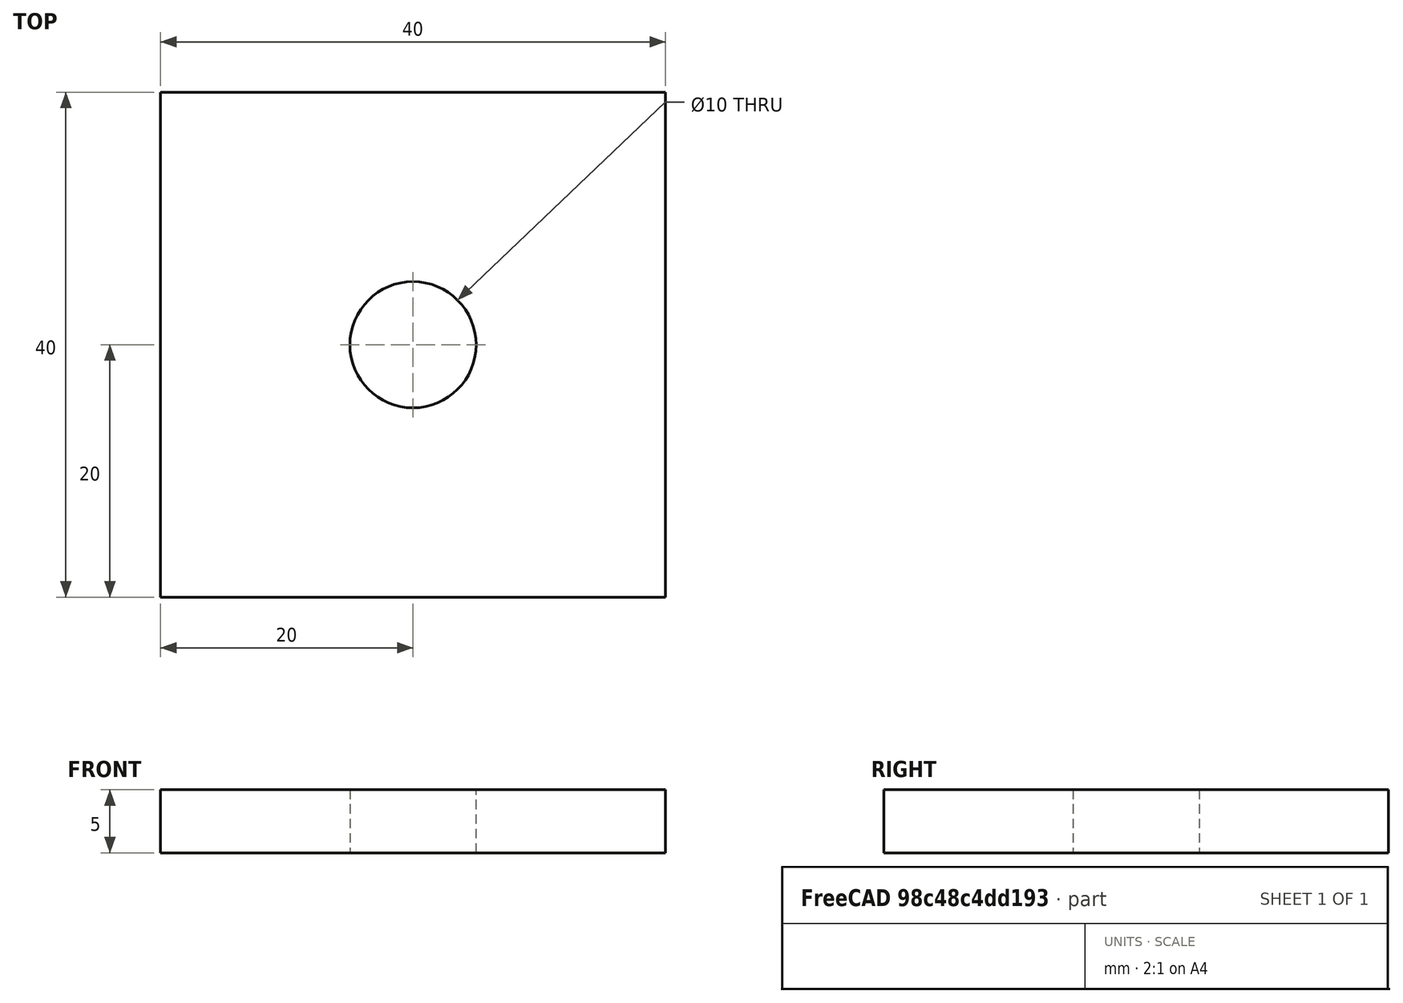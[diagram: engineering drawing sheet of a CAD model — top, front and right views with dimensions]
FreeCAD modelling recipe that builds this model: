
FCSTD DOCUMENT  (FreeCAD 0.20R29177 +233 (Git))
Label: L4-Ej3
License: Creative Commons Attribution-ShareAlike
LicenseURL: http://creativecommons.org/licenses/by-sa/4.0/
objects: Part::Extrusion×2, Sketcher::SketchObject×1
note: 3 computed .brp shape members not serialized (recipe doc carries the construction recipe); baked Part::Feature solids carry a one-line shape summary decoded from their .brp

FEATURE [Sketcher::SketchObject] Sketch
  FullyConstrained = true
  sketch-geometry (5):
    g0: LineSegment StartX=-20 StartY=20 StartZ=0 EndX=20 EndY=20 EndZ=0
    g1: LineSegment StartX=20 StartY=20 StartZ=0 EndX=20 EndY=-20 EndZ=0
    g2: LineSegment StartX=20 StartY=-20 StartZ=0 EndX=-20 EndY=-20 EndZ=0
    g3: LineSegment StartX=-20 StartY=-20 StartZ=0 EndX=-20 EndY=20 EndZ=0
    g4: Circle CenterX=0 CenterY=0 CenterZ=0 NormalX=0 NormalY=0 NormalZ=1 AngleXU=0 Radius=5
  constraints (13):
    c: Coincident(g0,g1)
    c: Coincident(g1,g2)
    c: Coincident(g2,g3)
    c: Coincident(g3,g0)
    c: Horizontal(g0)
    c: Horizontal(g2)
    c: Vertical(g1)
    c: Vertical(g3)
    c: Symmetric(g0,g1,g-1)
    c: Equal(g0,g1)
    c: Coincident(g4,g-1)
    c: Diameter(g4) = 10
    c: DistanceY(g1,g1) = 40
FEATURE [Part::Extrusion] Extrude
  Base = -> Sketch
  Dir = (0,0,1)
  DirMode = 2
  FaceMakerClass = Part::FaceMakerBullseye
  LengthFwd = 5
  LengthRev = 0
  Solid = true
  Symmetric = false
FEATURE [Part::Extrusion] Extrude001
  Base = -> Sketch
  Dir = (0,0,1)
  DirMode = 2
  FaceMakerClass = Part::FaceMakerBullseye
  LengthFwd = 5
  LengthRev = 0
  Solid = true
  Symmetric = false
